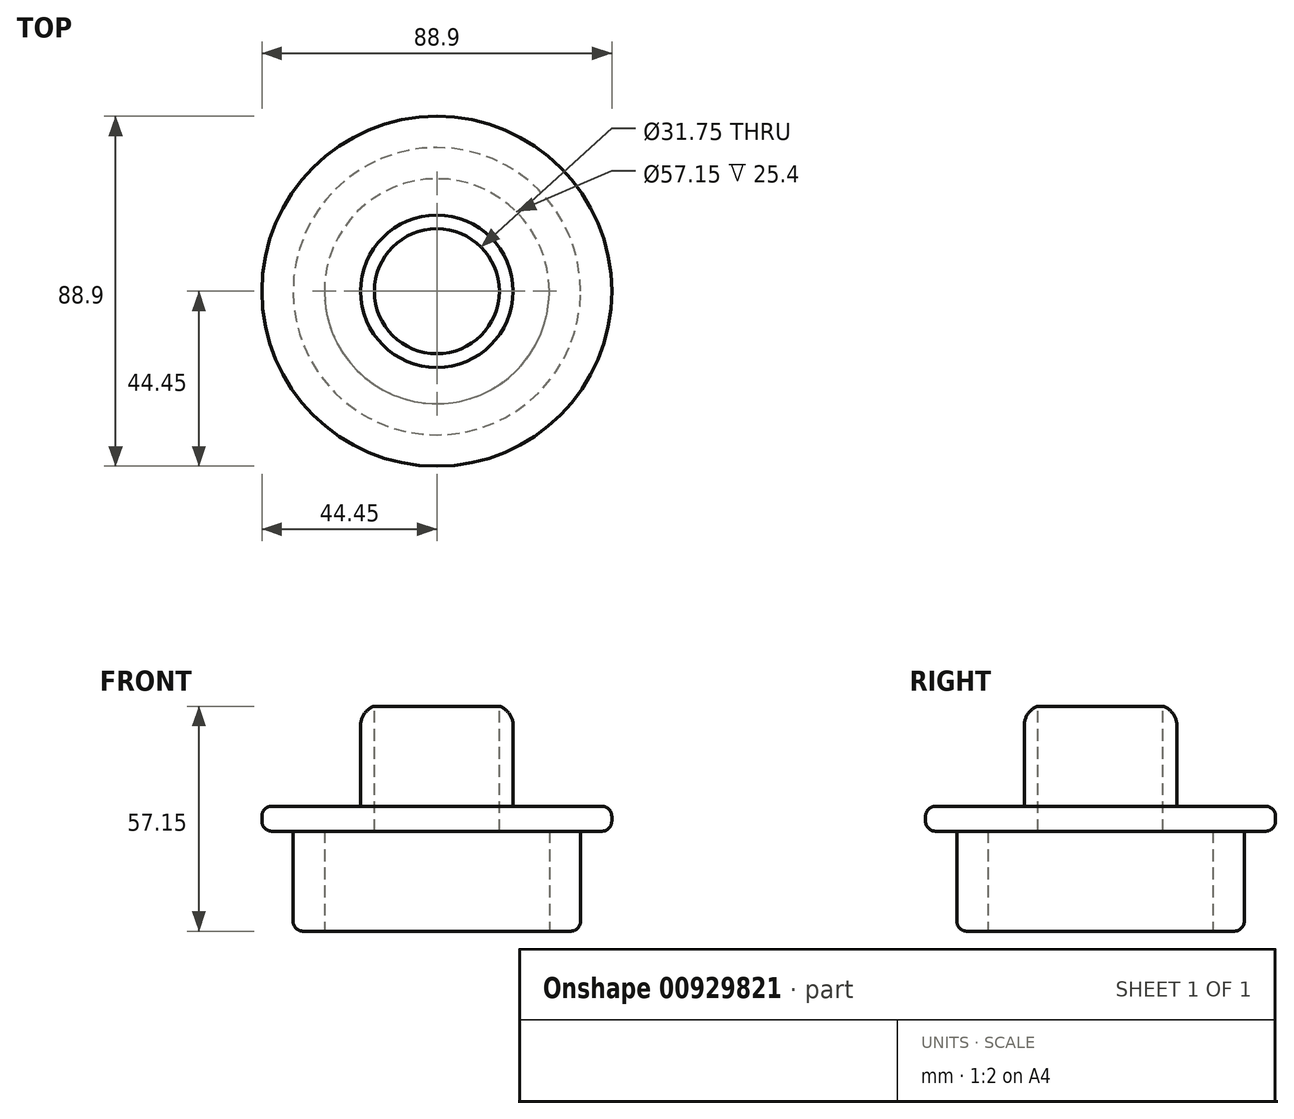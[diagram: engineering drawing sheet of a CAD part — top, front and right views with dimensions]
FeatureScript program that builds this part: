
annotation { "Feature Type Name" : "Feature", "Feature Type Description" : "" }
export const myFeature = defineFeature(function(context is Context, id is Id, definition is map)
    precondition{}
    {
        {
            var Q0;
            Q0=qCreatedBy(makeId("Top.planeOp"),FACE);
            var sketch = newSketch(context, id + "F0", { "sketchPlane" : qUnion([Q0])});
            skCircle(sketch, "E0", {"center": v(0, 0) * mm, "radius": 44.45 * mm});
            skSolve(sketch);
        }
        {
            var Q0;
            Q0 = qSketchRegion(id + "F0", true);
            extrude(context, id + "F1", {"entities" : qUnion([Q0]), "depth" : 6.35 * mm, "offsetDistance" : 25.4 * mm});
        }
        {
            var Q0;
            Q0=makeQuery(id+"F1.opExtrude","CAP_FACE",FACE,{"disambiguationData":[OSD([sQuery(id+"F0.wireOp",EDGE,"E0")])],"isStart":true});
            var sketch = newSketch(context, id + "F2", { "sketchPlane" : qUnion([Q0])});
            skCircle(sketch, "E1", {"center": v(0, 0) * mm, "radius": 36.51 * mm});
            skSolve(sketch);
        }
        {
            var Q0;
            Q0 = qSketchRegion(id + "F2", true);
            extrude(context, id + "F3", {"entities" : qUnion([Q0]), "operationType" : NewBodyOperationType.ADD, "depth" : 25.4 * mm, "offsetDistance" : 25.4 * mm});
        }
        {
            var Q0;
            Q0=makeQuery(id+"F1.opExtrude","CAP_FACE",FACE,{"disambiguationData":[OSD([sQuery(id+"F0.wireOp",EDGE,"E0")])],"isStart":false});
            var sketch = newSketch(context, id + "F4", { "sketchPlane" : qUnion([Q0])});
            skCircle(sketch, "E2", {"center": v(0, 0) * mm, "radius": 19.37 * mm});
            skSolve(sketch);
        }
        {
            var Q0;
            Q0 = qSketchRegion(id + "F4", true);
            extrude(context, id + "F5", {"entities" : qUnion([Q0]), "operationType" : NewBodyOperationType.ADD, "depth" : 25.4 * mm, "offsetDistance" : 25.4 * mm});
        }
        {
            var Q0;
            Q0=makeQuery(id+"F5.opExtrude","CAP_FACE",FACE,{"disambiguationData":[OSD([sQuery(id+"F4.wireOp",EDGE,"E2")])],"isStart":false});
            var sketch = newSketch(context, id + "F6", { "sketchPlane" : qUnion([Q0])});
            skCircle(sketch, "E3", {"center": v(0, 0) * mm, "radius": 15.88 * mm});
            skSolve(sketch);
        }
        {
            var Q0;
            Q0=makeQuery(id+"F6.imprint","IMPRINT",FACE,{"disambiguationData":[TD([[makeQuery(id+"F6.imprint","IMPRINT",EDGE,{"derivedFrom":sQuery(id+"F6.wireOp",EDGE,"E3")}),1.0]])]});
            var Q1;
            Q1=makeQuery(id+"F1.opExtrude","CAP_FACE",FACE,{"disambiguationData":[OSD([sQuery(id+"F0.wireOp",EDGE,"E0")])],"isStart":true});
            extrude(context, id + "F7", {"entities" : qUnion([Q0]), "operationType" : NewBodyOperationType.REMOVE, "endBound" : BoundingType.UP_TO_SURFACE, "oppositeDirection" : true, "depth" : 25.4 * mm, "endBoundEntityFace" : qUnion([Q1]), "offsetDistance" : 25.4 * mm});
        }
        {
            var Q0;
            Q0=makeQuery(id+"F3.opExtrude","CAP_FACE",FACE,{"disambiguationData":[OSD([sQuery(id+"F2.wireOp",EDGE,"E1")])],"isStart":false});
            var sketch = newSketch(context, id + "F8", { "sketchPlane" : qUnion([Q0])});
            skCircle(sketch, "E4", {"center": v(0, 0) * mm, "radius": 28.58 * mm});
            skSolve(sketch);
        }
        {
            var Q0;
            Q0=makeQuery(id+"F8.imprint","IMPRINT",FACE,{"disambiguationData":[TD([[makeQuery(id+"F8.imprint","IMPRINT",EDGE,{"derivedFrom":sQuery(id+"F8.wireOp",EDGE,"E4")}),1.0]])]});
            var Q1;
            Q1=makeQuery(id+"F1.opExtrude","CAP_FACE",FACE,{"disambiguationData":[OSD([sQuery(id+"F0.wireOp",EDGE,"E0")])],"isStart":true});
            extrude(context, id + "F9", {"entities" : qUnion([Q0]), "operationType" : NewBodyOperationType.REMOVE, "endBound" : BoundingType.UP_TO_SURFACE, "oppositeDirection" : true, "depth" : 25.4 * mm, "endBoundEntityFace" : qUnion([Q1]), "offsetDistance" : 25.4 * mm});
        }
        {
            var Q0;
            Q0=makeQuery(id+"F3.opExtrude","CAP_EDGE",EDGE,{"disambiguationData":[OSD([sQuery(id+"F2.wireOp",EDGE,"E1")])],"isStart":false});
            var Q1;
            Q1=makeQuery(id+"F9.boolean.opBoolean","COPY",EDGE,{"derivedFrom":makeQuery(id+"F9.opExtrude","CAP_EDGE",EDGE,{"disambiguationData":[OSD([sQuery(id+"F8.wireOp",EDGE,"E4")])],"isStart":true})});
            var Q2;
            Q2=makeQuery(id+"F7.boolean.opBoolean","COPY",EDGE,{"derivedFrom":makeQuery(id+"F7.opExtrude","CAP_EDGE",EDGE,{"disambiguationData":[OSD([sQuery(id+"F6.wireOp",EDGE,"E3")])],"isStart":false})});
            var Q3;
            Q3=makeQuery(id+"F7.boolean.opBoolean","COPY",EDGE,{"derivedFrom":makeQuery(id+"F7.opExtrude","CAP_EDGE",EDGE,{"disambiguationData":[OSD([sQuery(id+"F6.wireOp",EDGE,"E3")])],"isStart":true})});
            var Q4;
            Q4=makeQuery(id+"F3.opExtrude","CAP_EDGE",EDGE,{"disambiguationData":[OSD([sQuery(id+"F2.wireOp",EDGE,"E1")])],"isStart":true});
            var Q5;
            Q5=makeQuery(id+"F1.opExtrude","CAP_EDGE",EDGE,{"disambiguationData":[OSD([sQuery(id+"F0.wireOp",EDGE,"E0")])],"isStart":true});
            var Q6;
            Q6=makeQuery(id+"F1.opExtrude","CAP_EDGE",EDGE,{"disambiguationData":[OSD([sQuery(id+"F0.wireOp",EDGE,"E0")])],"isStart":false});
            var Q7;
            Q7=makeQuery(id+"F5.opExtrude","CAP_EDGE",EDGE,{"disambiguationData":[OSD([sQuery(id+"F4.wireOp",EDGE,"E2")])],"isStart":true});
            fillet(context, id + "F10", {"entities" : qUnion([Q0, Q1, Q2, Q3, Q4, Q5, Q6, Q7]), "radius" : 2.54 * mm, "tangentPropagation" : true, "allowEdgeOverflow" : false});
        }
        {
            var Q0;
            Q0=makeQuery(id+"F5.opExtrude","CAP_EDGE",EDGE,{"disambiguationData":[OSD([sQuery(id+"F4.wireOp",EDGE,"E2")])],"isStart":false});
            fillet(context, id + "F11", {"entities" : qUnion([Q0]), "radius" : 5.08 * mm, "tangentPropagation" : true, "allowEdgeOverflow" : false});
        }
    });
